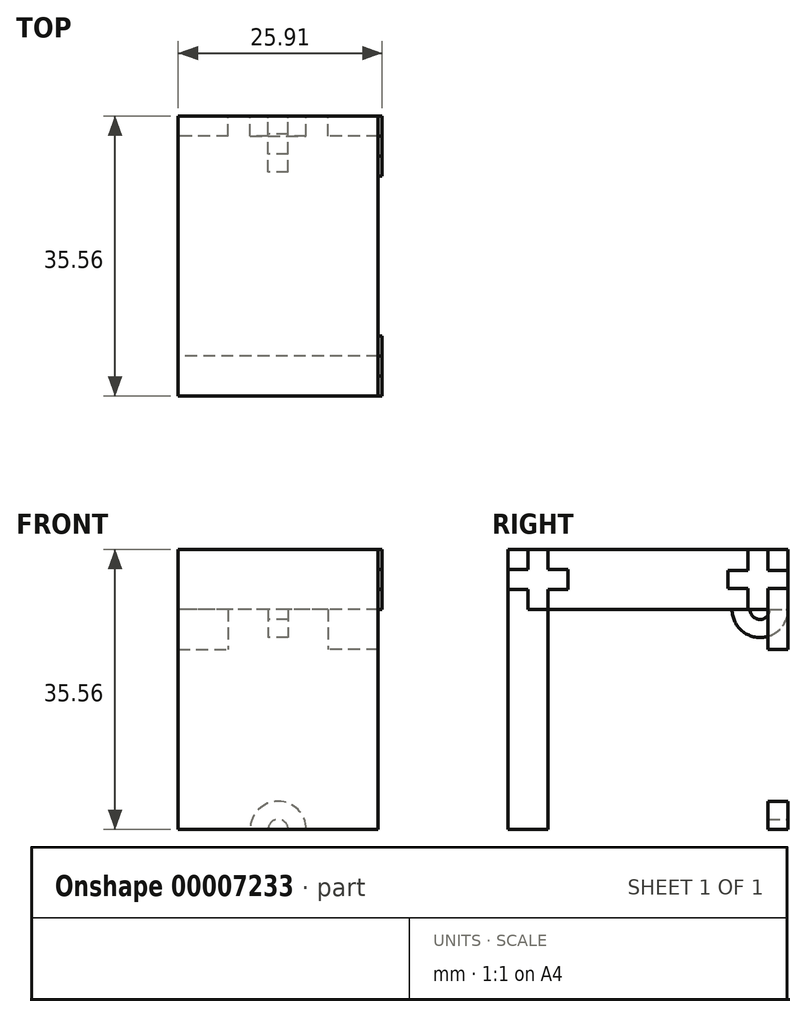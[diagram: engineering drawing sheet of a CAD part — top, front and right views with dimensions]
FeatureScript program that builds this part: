
annotation { "Feature Type Name" : "Feature", "Feature Type Description" : "" }
export const myFeature = defineFeature(function(context is Context, id is Id, definition is map)
    precondition{}
    {
        {
            var Q0;
            Q0=qCreatedBy(makeId("Right.planeOp"),FACE);
            var sketch = newSketch(context, id + "F0", { "sketchPlane" : qUnion([Q0])});
            skLineSegment(sketch, "E0", {"start": v(5.08, 33.02) * mm, "end": v(33.02, 33.02) * mm});
            skLineSegment(sketch, "E1", {"start": v(35.56, 33.02) * mm, "end": v(35.56, 40.64) * mm});
            skLineSegment(sketch, "E2", {"start": v(35.56, 40.64) * mm, "end": v(0, 40.64) * mm});
            skLineSegment(sketch, "E3", {"start": v(0, 40.64) * mm, "end": v(0, 5.08) * mm});
            skLineSegment(sketch, "E4", {"start": v(0, 0) * mm, "end": v(55.88, 0) * mm});
            skLineSegment(sketch, "E5", {"start": v(5.08, 33.02) * mm, "end": v(5.08, 5.08) * mm});
            skLineSegment(sketch, "E6", {"start": v(5.08, 5.08) * mm, "end": v(55.88, 5.08) * mm});
            skLineSegment(sketch, "E7", {"start": v(55.88, 5.08) * mm, "end": v(55.88, 0) * mm});
            skPoint(sketch, "E8", {"position": v(33.02, 33.02) * mm});
            skPoint(sketch, "E9", {"position": v(0, 33.02) * mm});
            skPoint(sketch, "E10", {"position": v(0, 5.08) * mm});
            skLineSegment(sketch, "E11", {"start": v(0, 5.08) * mm, "end": v(-29.94, 5.08) * mm});
            skLineSegment(sketch, "E12", {"start": v(-29.94, 5.08) * mm, "end": v(-29.94, 0) * mm});
            skLineSegment(sketch, "E13", {"start": v(-29.94, 0) * mm, "end": v(0, 0) * mm});
            skPoint(sketch, "E14.end.orphan", {"position": v(35.56, 25.4) * mm});
            skLineSegment(sketch, "E15", {"start": v(33.02, 33.02) * mm, "end": v(35.56, 33.02) * mm});
            skLineSegment(sketch, "E16", {"start": v(0, 5.08) * mm, "end": v(5.08, 5.08) * mm});
            skSolve(sketch);
        }
        {
            var Q0;
            Q0=makeQuery(id+"F0.imprint","IMPRINT",FACE,{"disambiguationData":[TD([[makeQuery(id+"F0.imprint","IMPRINT",EDGE,{"derivedFrom":sQuery(id+"F0.wireOp",EDGE,"E0")}),1.0]])]});
            extrude(context, id + "F1", {"entities" : qUnion([Q0]), "depth" : 25.4 * mm, "offsetDistance" : 25 * mm});
        }
        {
            var Q0;
            Q0=makeQuery(id+"F1.opExtrude","CAP_FACE",FACE,{"disambiguationData":[OSD([sQuery(id+"F0.wireOp",EDGE,"E0"),sQuery(id+"F0.wireOp",EDGE,"E1"),sQuery(id+"F0.wireOp",EDGE,"E2"),sQuery(id+"F0.wireOp",EDGE,"E3"),sQuery(id+"F0.wireOp",EDGE,"E4"),sQuery(id+"F0.wireOp",EDGE,"E5"),sQuery(id+"F0.wireOp",EDGE,"E6"),sQuery(id+"F0.wireOp",EDGE,"E7"),sQuery(id+"F0.wireOp",EDGE,"E11"),sQuery(id+"F0.wireOp",EDGE,"E12"),sQuery(id+"F0.wireOp",EDGE,"E13"),sQuery(id+"F0.wireOp",EDGE,"E15")])],"isStart":false});
            var sketch = newSketch(context, id + "F2", { "sketchPlane" : qUnion([Q0])});
            skArc(sketch, "E17", {"start": v(28.45, 33.02) * mm, "mid": v(32, 29.46) * mm, "end": v(35.56, 33.02) * mm});
            skArc(sketch, "E18", {"start": v(30.73, 33.02) * mm, "mid": v(32, 31.75) * mm, "end": v(33.27, 33.02) * mm});
            skLineSegment(sketch, "E19", {"start": v(30.73, 33.02) * mm, "end": v(28.45, 33.02) * mm});
            skLineSegment(sketch, "E20", {"start": v(28.45, 33.02) * mm, "end": v(30.73, 33.02) * mm});
            skLineSegment(sketch, "E21", {"start": v(33.27, 33.02) * mm, "end": v(35.56, 33.02) * mm});
            skSolve(sketch);
        }
        {
            var Q0;
            Q0=qSketchRegion(id+"F2",true);
            extrude(context, id + "F3", {"entities" : qUnion([Q0]), "depth" : 2.54 * mm});
        }
        {
            var Q0;
            Q0=makeQuery(id+"F3.opExtrude","SWEPT_BODY",BODY,{"disambiguationData":[OSD([sQuery(id+"F2.wireOp",EDGE,"E17"),sQuery(id+"F2.wireOp",EDGE,"E18"),sQuery(id+"F2.wireOp",EDGE,"E20"),sQuery(id+"F2.wireOp",EDGE,"E21")])]});
            var Q1;
            Q1=makeQuery(id+"F1.opExtrude","SWEPT_EDGE",EDGE,{"disambiguationData":[OSD([sQuery(id+"F0.wireOp",EDGE,"E1"),sQuery(id+"F0.wireOp",EDGE,"E15")])]});
            transform(context, id + "F4", {"entities" : qUnion([Q0]), "transformType" : TransformType.TRANSLATION_DISTANCE, "transformDirection" : qUnion([Q1]), "distance" : 13.97 * mm, "makeCopy" : false});
        }
        {
            var Q0;
            Q0=makeQuery(id+"F1.opExtrude","SWEPT_FACE",FACE,{"disambiguationData":[OSD([sQuery(id+"F0.wireOp",EDGE,"E1")])]});
            var sketch = newSketch(context, id + "F5", { "sketchPlane" : qUnion([Q0])});
            skArc(sketch, "E22", {"start": v(-9.14, 5.08) * mm, "mid": v(-12.7, 8.64) * mm, "end": v(-16.26, 5.08) * mm});
            skArc(sketch, "E23", {"start": v(-11.43, 5.08) * mm, "mid": v(-12.7, 6.35) * mm, "end": v(-13.97, 5.08) * mm});
            skLineSegment(sketch, "E24", {"start": v(-16.26, 5.08) * mm, "end": v(-13.97, 5.08) * mm});
            skLineSegment(sketch, "E25", {"start": v(-11.43, 5.08) * mm, "end": v(-9.14, 5.08) * mm});
            skSolve(sketch);
        }
        {
            var Q0;
            Q0=qSketchRegion(id+"F5",true);
            extrude(context, id + "F6", {"entities" : qUnion([Q0]), "oppositeDirection" : true, "depth" : 2.54 * mm});
        }
        {
            var Q0;
            Q0=makeQuery(id+"F1.opExtrude","SWEPT_FACE",FACE,{"disambiguationData":[OSD([sQuery(id+"F0.wireOp",EDGE,"E1")])]});
            var sketch = newSketch(context, id + "F7", { "sketchPlane" : qUnion([Q0])});
            skLineSegment(sketch, "E26.bottom", {"start": v(-25.4, 33.02) * mm, "end": v(-19.05, 33.02) * mm});
            skLineSegment(sketch, "E26.top", {"start": v(-25.4, 27.94) * mm, "end": v(-19.05, 27.94) * mm});
            skLineSegment(sketch, "E26.left", {"start": v(-25.4, 33.02) * mm, "end": v(-25.4, 27.94) * mm});
            skLineSegment(sketch, "E26.right", {"start": v(-19.05, 33.02) * mm, "end": v(-19.05, 27.94) * mm});
            skLineSegment(sketch, "E27.bottom", {"start": v(0, 33.02) * mm, "end": v(-6.35, 33.02) * mm});
            skLineSegment(sketch, "E27.top", {"start": v(0, 27.94) * mm, "end": v(-6.35, 27.94) * mm});
            skLineSegment(sketch, "E27.left", {"start": v(0, 33.02) * mm, "end": v(0, 27.94) * mm});
            skLineSegment(sketch, "E27.right", {"start": v(-6.35, 33.02) * mm, "end": v(-6.35, 27.94) * mm});
            skLineSegment(sketch, "E28", {"start": v(-12.7, 33.02) * mm, "end": v(-12.7, 12.44) * mm, "construction": true});
            skSolve(sketch);
        }
        {
            var Q0;
            Q0=qSketchRegion(id+"F7",true);
            extrude(context, id + "F8", {"entities" : qUnion([Q0]), "oppositeDirection" : true, "depth" : 2.54 * mm});
        }
        {
            var Q0;
            Q0=makeQuery(id+"F1.opExtrude","SWEPT_BODY",BODY,{"disambiguationData":[OSD([sQuery(id+"F0.wireOp",EDGE,"E0"),sQuery(id+"F0.wireOp",EDGE,"E1"),sQuery(id+"F0.wireOp",EDGE,"E2"),sQuery(id+"F0.wireOp",EDGE,"E3"),sQuery(id+"F0.wireOp",EDGE,"E4"),sQuery(id+"F0.wireOp",EDGE,"E5"),sQuery(id+"F0.wireOp",EDGE,"E6"),sQuery(id+"F0.wireOp",EDGE,"E7"),sQuery(id+"F0.wireOp",EDGE,"E11"),sQuery(id+"F0.wireOp",EDGE,"E12"),sQuery(id+"F0.wireOp",EDGE,"E13"),sQuery(id+"F0.wireOp",EDGE,"E15")])]});
            var Q1;
            Q1=makeQuery(id+"F3.opExtrude","SWEPT_BODY",BODY,{"disambiguationData":[OSD([sQuery(id+"F2.wireOp",EDGE,"E17"),sQuery(id+"F2.wireOp",EDGE,"E18"),sQuery(id+"F2.wireOp",EDGE,"E20"),sQuery(id+"F2.wireOp",EDGE,"E21")])]});
            var Q2;
            Q2=makeQuery(id+"F8.opExtrude","SWEPT_BODY",BODY,{"disambiguationData":[OSD([sQuery(id+"F7.wireOp",EDGE,"E27.bottom"),sQuery(id+"F7.wireOp",EDGE,"E27.top"),sQuery(id+"F7.wireOp",EDGE,"E27.left"),sQuery(id+"F7.wireOp",EDGE,"E27.right")])]});
            var Q3;
            Q3=makeQuery(id+"F8.opExtrude","SWEPT_BODY",BODY,{"disambiguationData":[OSD([sQuery(id+"F7.wireOp",EDGE,"E26.bottom"),sQuery(id+"F7.wireOp",EDGE,"E26.top"),sQuery(id+"F7.wireOp",EDGE,"E26.left"),sQuery(id+"F7.wireOp",EDGE,"E26.right")])]});
            var Q4;
            Q4=makeQuery(id+"F6.opExtrude","SWEPT_BODY",BODY,{"disambiguationData":[OSD([sQuery(id+"F5.wireOp",EDGE,"E22"),sQuery(id+"F5.wireOp",EDGE,"E23"),sQuery(id+"F5.wireOp",EDGE,"E24"),sQuery(id+"F5.wireOp",EDGE,"E25")])]});
            booleanBodies(context, id + "F9", {"operationType" : BooleanOperationType.UNION, "tools" : qUnion([Q0, Q1, Q2, Q3, Q4])});
        }
        {
            var Q0;
            Q0=makeQuery(id+"F9.opBoolean","MERGE",FACE,{"derivedFrom":[makeQuery(id+"F1.opExtrude","CAP_FACE",FACE,{"disambiguationData":[OSD([sQuery(id+"F0.wireOp",EDGE,"E0"),sQuery(id+"F0.wireOp",EDGE,"E1"),sQuery(id+"F0.wireOp",EDGE,"E2"),sQuery(id+"F0.wireOp",EDGE,"E3"),sQuery(id+"F0.wireOp",EDGE,"E4"),sQuery(id+"F0.wireOp",EDGE,"E5"),sQuery(id+"F0.wireOp",EDGE,"E6"),sQuery(id+"F0.wireOp",EDGE,"E7"),sQuery(id+"F0.wireOp",EDGE,"E11"),sQuery(id+"F0.wireOp",EDGE,"E12"),sQuery(id+"F0.wireOp",EDGE,"E13"),sQuery(id+"F0.wireOp",EDGE,"E15")])],"isStart":false}),makeQuery(id+"F8.opExtrude","SWEPT_FACE",FACE,{"disambiguationData":[OSD([sQuery(id+"F7.wireOp",EDGE,"E26.left")])]})]});
            var sketch = newSketch(context, id + "F10", { "sketchPlane" : qUnion([Q0])});
            skLineSegment(sketch, "E29", {"start": v(17.78, 40.64) * mm, "end": v(17.78, 33.02) * mm, "construction": true});
            skLineSegment(sketch, "E30.bottom", {"start": v(0, 38.1) * mm, "end": v(2.54, 38.1) * mm});
            skLineSegment(sketch, "E30.top", {"start": v(0, 35.56) * mm, "end": v(2.54, 35.56) * mm});
            skLineSegment(sketch, "E30.left", {"start": v(0, 38.1) * mm, "end": v(0, 35.56) * mm});
            skLineSegment(sketch, "E30.right", {"start": v(7.62, 38.1) * mm, "end": v(7.62, 35.56) * mm});
            skLineSegment(sketch, "E31.bottom", {"start": v(27.94, 37.97) * mm, "end": v(30.48, 37.97) * mm});
            skLineSegment(sketch, "E31.top", {"start": v(27.94, 35.71) * mm, "end": v(30.48, 35.71) * mm});
            skLineSegment(sketch, "E31.left", {"start": v(27.94, 37.97) * mm, "end": v(27.94, 35.71) * mm});
            skLineSegment(sketch, "E31.right", {"start": v(35.56, 37.97) * mm, "end": v(35.56, 35.71) * mm});
            skLineSegment(sketch, "E32.bottom", {"start": v(2.54, 40.64) * mm, "end": v(5.08, 40.64) * mm});
            skLineSegment(sketch, "E32.top", {"start": v(2.54, 33.02) * mm, "end": v(5.08, 33.02) * mm});
            skLineSegment(sketch, "E32.left", {"start": v(2.54, 40.64) * mm, "end": v(2.54, 38.1) * mm});
            skLineSegment(sketch, "E32.right", {"start": v(5.08, 40.64) * mm, "end": v(5.08, 38.1) * mm});
            skLineSegment(sketch, "E33.bottom", {"start": v(30.48, 40.64) * mm, "end": v(33.02, 40.64) * mm});
            skLineSegment(sketch, "E33.top", {"start": v(30.48, 33.02) * mm, "end": v(33.02, 33.02) * mm});
            skLineSegment(sketch, "E33.left", {"start": v(30.48, 40.64) * mm, "end": v(30.48, 37.97) * mm});
            skLineSegment(sketch, "E33.right", {"start": v(33.02, 40.64) * mm, "end": v(33.02, 37.97) * mm});
            skPoint(sketch, "E34", {"position": v(2.54, 38.1) * mm});
            skPoint(sketch, "E35", {"position": v(5.08, 38.1) * mm});
            skPoint(sketch, "E36", {"position": v(5.08, 35.56) * mm});
            skPoint(sketch, "E37", {"position": v(2.54, 35.56) * mm});
            skPoint(sketch, "E38", {"position": v(30.48, 37.97) * mm});
            skPoint(sketch, "E39", {"position": v(33.02, 37.97) * mm});
            skPoint(sketch, "E40", {"position": v(33.02, 35.71) * mm});
            skPoint(sketch, "E41", {"position": v(30.48, 35.71) * mm});
            skLineSegment(sketch, "E42.trimOffspring", {"start": v(5.08, 35.56) * mm, "end": v(5.08, 33.02) * mm});
            skLineSegment(sketch, "E43.trimOffspring", {"start": v(5.08, 38.1) * mm, "end": v(7.62, 38.1) * mm});
            skLineSegment(sketch, "E44.trimOffspring", {"start": v(2.54, 35.56) * mm, "end": v(2.54, 33.02) * mm});
            skLineSegment(sketch, "E45.trimOffspring", {"start": v(5.08, 35.56) * mm, "end": v(7.62, 35.56) * mm});
            skLineSegment(sketch, "E46.trimOffspring", {"start": v(33.02, 37.97) * mm, "end": v(35.56, 37.97) * mm});
            skLineSegment(sketch, "E47.trimOffspring", {"start": v(30.48, 35.71) * mm, "end": v(30.48, 33.02) * mm});
            skLineSegment(sketch, "E48.trimOffspring", {"start": v(33.02, 35.71) * mm, "end": v(35.56, 35.71) * mm});
            skLineSegment(sketch, "E49.trimOffspring", {"start": v(33.02, 35.71) * mm, "end": v(33.02, 33.02) * mm});
            skSolve(sketch);
        }
        {
            var Q0;
            Q0=qSketchRegion(id+"F10",true);
            extrude(context, id + "F11", {"entities" : qUnion([Q0]), "depth" : 0.5 * mm});
        }
    });
